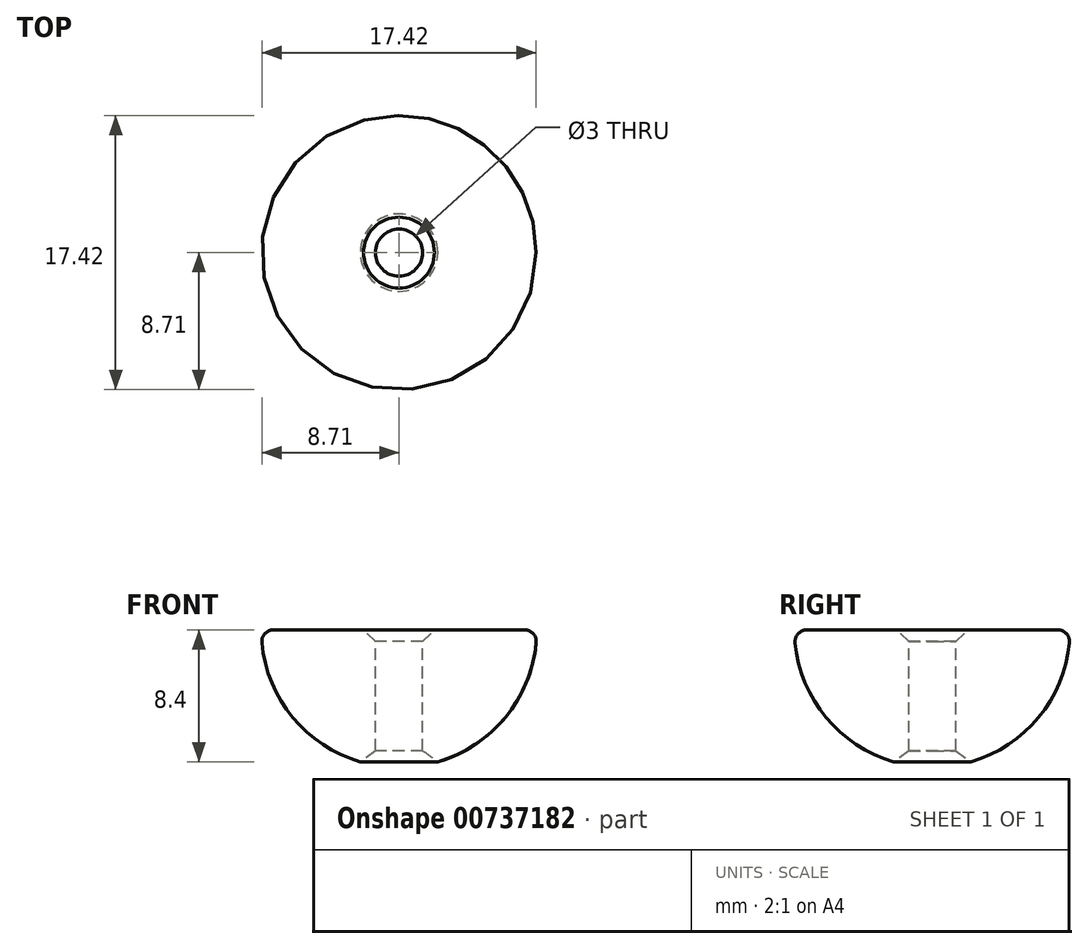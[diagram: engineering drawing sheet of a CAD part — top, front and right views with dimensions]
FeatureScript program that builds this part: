
annotation { "Feature Type Name" : "Feature", "Feature Type Description" : "" }
export const myFeature = defineFeature(function(context is Context, id is Id, definition is map)
    precondition{}
    {
        {
            var Q0;
            Q0=qCreatedBy(makeId("Front.planeOp"),FACE);
            var sketch = newSketch(context, id + "F0", { "sketchPlane" : qUnion([Q0])});
            skArc(sketch, "E0", {"start": v(1.5, -8.62) * mm, "mid": v(6.7, -5.63) * mm, "end": v(8.75, 0) * mm});
            skPoint(sketch, "E1.orphan", {"position": v(-8.75, 0) * mm});
            skLineSegment(sketch, "E2", {"start": v(1.5, 0) * mm, "end": v(1.5, -8.62) * mm});
            skLineSegment(sketch, "E3", {"start": v(1.5, 0) * mm, "end": v(8.75, 0) * mm});
            skLineSegment(sketch, "E4", {"start": v(0, -3.73) * mm, "end": v(0, -5.41) * mm});
            skSolve(sketch);
        }
        {
            var Q0;
            Q0=makeQuery(id+"F0.imprint","IMPRINT",FACE,{"disambiguationData":[TD([[makeQuery(id+"F0.imprint","IMPRINT",EDGE,{"derivedFrom":sQuery(id+"F0.wireOp",EDGE,"E0")}),1.0]])]});
            var Q1;
            Q1=sQuery(id+"F0.wireOp",EDGE,"E4");
            revolve(context, id + "F1", {"surfaceOperationType" : NewSurfaceOperationType.NEW, "entities" : qUnion([Q0]), "axis" : qUnion([Q1]), "revolveType" : RevolveType.FULL});
        }
        {
            var Q0;
            Q0=makeQuery(id+"F1.opRevolve","SWEPT_EDGE",EDGE,{"disambiguationData":[OSD([sQuery(id+"F0.wireOp",EDGE,"E0"),sQuery(id+"F0.wireOp",EDGE,"E3")])]});
            fillet(context, id + "F2", {"entities" : qUnion([Q0]), "radius" : .75 * mm, "tangentPropagation" : true, "allowEdgeOverflow" : false});
        }
        {
            var Q0;
            Q0=makeQuery(id+"F1.opRevolve","SWEPT_EDGE",EDGE,{"disambiguationData":[OSD([sQuery(id+"F0.wireOp",EDGE,"E0"),sQuery(id+"F0.wireOp",EDGE,"E2")])]});
            var Q1;
            Q1=makeQuery(id+"F1.opRevolve","SWEPT_EDGE",EDGE,{"disambiguationData":[OSD([sQuery(id+"F0.wireOp",EDGE,"E2"),sQuery(id+"F0.wireOp",EDGE,"E3")])]});
            chamfer(context, id + "F3", {"entities" : qUnion([Q0, Q1]), "width" : .75 * mm});
        }
    });
